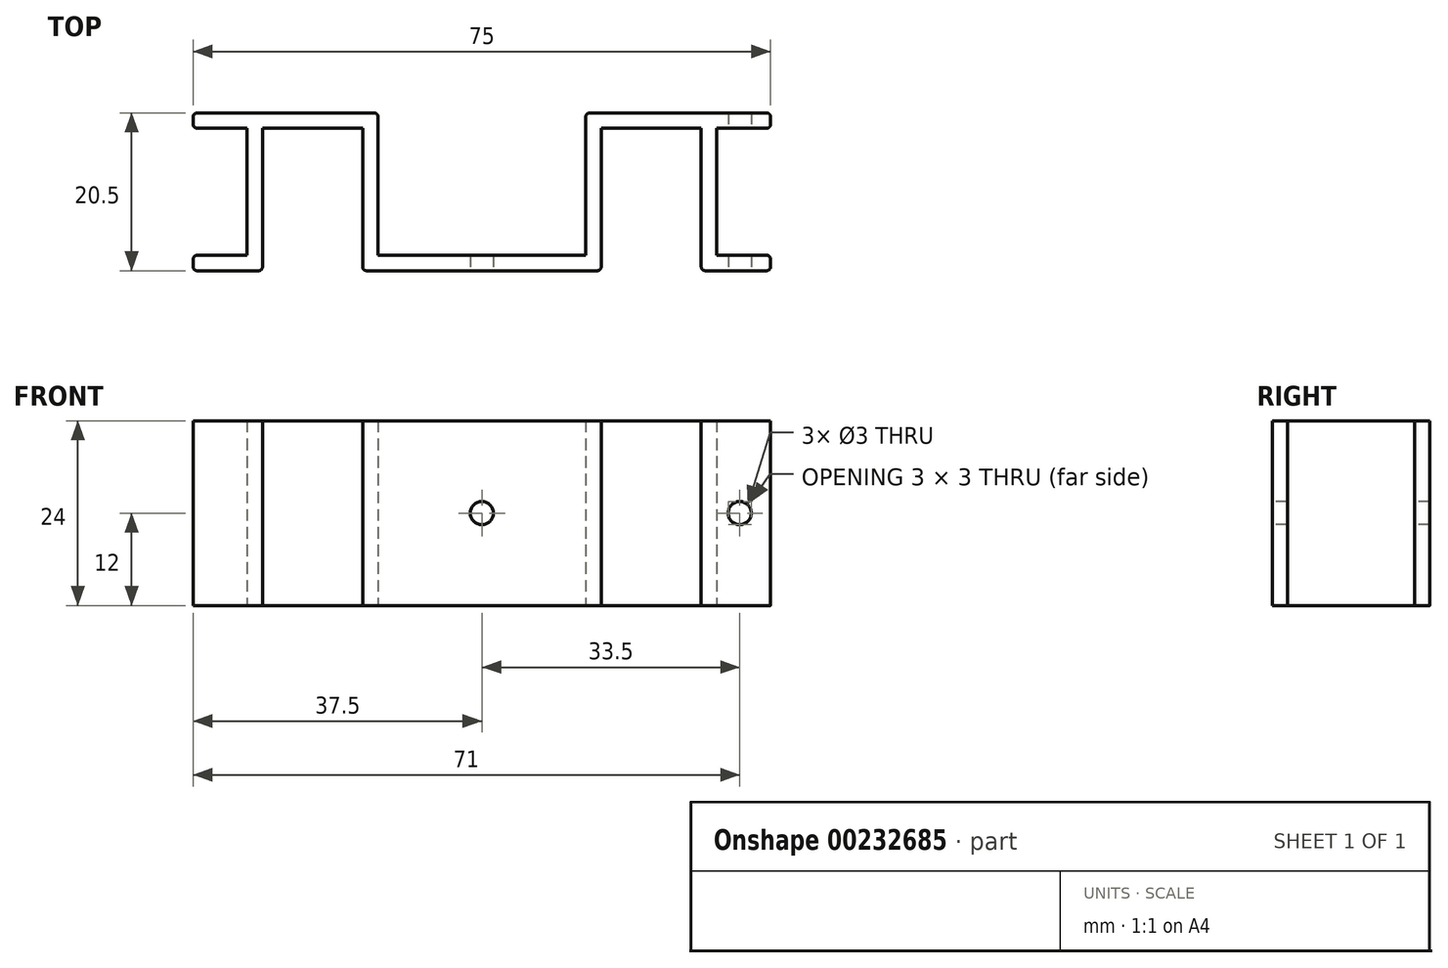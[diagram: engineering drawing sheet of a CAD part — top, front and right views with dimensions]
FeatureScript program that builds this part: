
annotation { "Feature Type Name" : "Feature", "Feature Type Description" : "" }
export const myFeature = defineFeature(function(context is Context, id is Id, definition is map)
    precondition{}
    {
        {
            var Q0;
            Q0=qCreatedBy(makeId("Top.planeOp"),FACE);
            var sketch = newSketch(context, id + "F0", { "sketchPlane" : qUnion([Q0])});
            skLineSegment(sketch, "E0", {"start": v(0, 0) * mm, "end": v(15.5, 0) * mm});
            skLineSegment(sketch, "E1", {"start": v(13.5, 20.5) * mm, "end": v(37.5, 20.5) * mm});
            skLineSegment(sketch, "E2", {"start": v(37.5, 20.5) * mm, "end": v(37.5, 18.5) * mm});
            skLineSegment(sketch, "E3", {"start": v(37.5, 18.5) * mm, "end": v(30.5, 18.5) * mm});
            skLineSegment(sketch, "E4", {"start": v(30.5, 18.5) * mm, "end": v(30.5, 2) * mm});
            skLineSegment(sketch, "E5", {"start": v(30.5, 2) * mm, "end": v(37.5, 2) * mm});
            skLineSegment(sketch, "E6", {"start": v(37.5, 2) * mm, "end": v(37.5, 0) * mm});
            skLineSegment(sketch, "E7", {"start": v(37.5, 0) * mm, "end": v(28.5, 0) * mm});
            skLineSegment(sketch, "E8", {"start": v(28.5, 0) * mm, "end": v(28.5, 18.5) * mm});
            skLineSegment(sketch, "E9", {"start": v(28.5, 18.5) * mm, "end": v(15.5, 18.5) * mm});
            skLineSegment(sketch, "E10", {"start": v(15.5, 18.5) * mm, "end": v(15.5, 0) * mm});
            skLineSegment(sketch, "E11", {"start": v(13.5, 2) * mm, "end": v(0, 2) * mm});
            skLineSegment(sketch, "E12", {"start": v(13.5, 2) * mm, "end": v(13.5, 20.5) * mm});
            skLineSegment(sketch, "E13.MirrorCS", {"start": v(0, 0) * mm, "end": v(-15.5, 0) * mm});
            skLineSegment(sketch, "E14.MirrorCS", {"start": v(-28.5, 18.5) * mm, "end": v(-15.5, 18.5) * mm});
            skLineSegment(sketch, "E15.MirrorCS", {"start": v(-37.5, 18.5) * mm, "end": v(-30.5, 18.5) * mm});
            skLineSegment(sketch, "E16.MirrorCS", {"start": v(-30.5, 2) * mm, "end": v(-37.5, 2) * mm});
            skLineSegment(sketch, "E17.MirrorCS", {"start": v(-15.5, 18.5) * mm, "end": v(-15.5, 0) * mm});
            skLineSegment(sketch, "E18.MirrorCS", {"start": v(-37.5, 2) * mm, "end": v(-37.5, 0) * mm});
            skLineSegment(sketch, "E19.MirrorCS", {"start": v(-37.5, 20.5) * mm, "end": v(-37.5, 18.5) * mm});
            skLineSegment(sketch, "E20.MirrorCS", {"start": v(-13.5, 2) * mm, "end": v(0, 2) * mm});
            skLineSegment(sketch, "E21.MirrorCS", {"start": v(-30.5, 18.5) * mm, "end": v(-30.5, 2) * mm});
            skLineSegment(sketch, "E22.MirrorCS", {"start": v(-28.5, 0) * mm, "end": v(-28.5, 18.5) * mm});
            skLineSegment(sketch, "E23.MirrorCS", {"start": v(-13.5, 2) * mm, "end": v(-13.5, 20.5) * mm});
            skLineSegment(sketch, "E24.MirrorCS", {"start": v(-13.5, 20.5) * mm, "end": v(-37.5, 20.5) * mm});
            skLineSegment(sketch, "E25.MirrorCS", {"start": v(-37.5, 0) * mm, "end": v(-28.5, 0) * mm});
            skPoint(sketch, "E26.orphan", {"position": v(0, 2) * mm});
            skSolve(sketch);
        }
        {
            var Q0;
            Q0=makeQuery(id+"F0.imprint","IMPRINT",FACE,{"disambiguationData":[TD([[makeQuery(id+"F0.imprint","IMPRINT",EDGE,{"derivedFrom":sQuery(id+"F0.wireOp",EDGE,"E0")}),1.0]])]});
            extrude(context, id + "F1", {"entities" : qUnion([Q0]), "depth" : 24 * mm});
        }
        {
            var Q0;
            Q0=makeQuery(id+"F1.opExtrude","SWEPT_FACE",FACE,{"disambiguationData":[OSD([sQuery(id+"F0.wireOp",EDGE,"E7")])]});
            var sketch = newSketch(context, id + "F2", { "sketchPlane" : qUnion([Q0])});
            skCircle(sketch, "E27", {"center": v(33.5, 12) * mm, "radius": 1.5 * mm});
            skCircle(sketch, "E28", {"center": v(0, 12) * mm, "radius": 1.5 * mm});
            skCircle(sketch, "E29.MirrorC", {"center": v(-33.5, 12) * mm, "radius": 1.5 * mm});
            skLineSegment(sketch, "E30", {"start": v(-41.57, 12) * mm, "end": v(-33.43, 12) * mm, "construction": true});
            skPoint(sketch, "E31", {"position": v(37.5, 12) * mm});
            skSolve(sketch);
        }
        {
            var Q0;
            Q0=makeQuery(id+"F2.imprint","IMPRINT",FACE,{"disambiguationData":[TD([[makeQuery(id+"F2.imprint","IMPRINT",EDGE,{"derivedFrom":sQuery(id+"F2.wireOp",EDGE,"E29.MirrorC")}),-1.0]])]});
            var Q1;
            Q1=makeQuery(id+"F2.imprint","IMPRINT",FACE,{"disambiguationData":[TD([[makeQuery(id+"F2.imprint","IMPRINT",EDGE,{"derivedFrom":sQuery(id+"F2.wireOp",EDGE,"E28")}),1.0]])]});
            var Q2;
            Q2=makeQuery(id+"F2.imprint","IMPRINT",FACE,{"disambiguationData":[TD([[makeQuery(id+"F2.imprint","IMPRINT",EDGE,{"derivedFrom":sQuery(id+"F2.wireOp",EDGE,"E27")}),1.0]])]});
            extrude(context, id + "F3", {"entities" : qUnion([Q0, Q1, Q2]), "operationType" : NewBodyOperationType.REMOVE, "oppositeDirection" : true, "depth" : 25 * mm});
        }
        {
            var Q0;
            Q0=makeQuery(id+"F1.opExtrude","SWEPT_EDGE",EDGE,{"disambiguationData":[OSD([sQuery(id+"F0.wireOp",EDGE,"E23.MirrorCS"),sQuery(id+"F0.wireOp",EDGE,"E24.MirrorCS")])]});
            var Q1;
            Q1=makeQuery(id+"F1.opExtrude","SWEPT_EDGE",EDGE,{"disambiguationData":[OSD([sQuery(id+"F0.wireOp",EDGE,"E1"),sQuery(id+"F0.wireOp",EDGE,"E12")])]});
            var Q2;
            Q2=makeQuery(id+"F1.opExtrude","SWEPT_EDGE",EDGE,{"disambiguationData":[OSD([sQuery(id+"F0.wireOp",EDGE,"E0"),sQuery(id+"F0.wireOp",EDGE,"E10")])]});
            var Q3;
            Q3=makeQuery(id+"F1.opExtrude","SWEPT_EDGE",EDGE,{"disambiguationData":[OSD([sQuery(id+"F0.wireOp",EDGE,"E22.MirrorCS"),sQuery(id+"F0.wireOp",EDGE,"E25.MirrorCS")])]});
            var Q4;
            Q4=makeQuery(id+"F1.opExtrude","SWEPT_EDGE",EDGE,{"disambiguationData":[OSD([sQuery(id+"F0.wireOp",EDGE,"E13.MirrorCS"),sQuery(id+"F0.wireOp",EDGE,"E17.MirrorCS")])]});
            var Q5;
            Q5=makeQuery(id+"F1.opExtrude","SWEPT_EDGE",EDGE,{"disambiguationData":[OSD([sQuery(id+"F0.wireOp",EDGE,"E7"),sQuery(id+"F0.wireOp",EDGE,"E8")])]});
            var Q6;
            Q6=makeQuery(id+"F1.opExtrude","SWEPT_EDGE",EDGE,{"disambiguationData":[OSD([sQuery(id+"F0.wireOp",EDGE,"E1"),sQuery(id+"F0.wireOp",EDGE,"E2")])]});
            var Q7;
            Q7=makeQuery(id+"F1.opExtrude","SWEPT_EDGE",EDGE,{"disambiguationData":[OSD([sQuery(id+"F0.wireOp",EDGE,"E2"),sQuery(id+"F0.wireOp",EDGE,"E3")])]});
            var Q8;
            Q8=makeQuery(id+"F1.opExtrude","SWEPT_EDGE",EDGE,{"disambiguationData":[OSD([sQuery(id+"F0.wireOp",EDGE,"E5"),sQuery(id+"F0.wireOp",EDGE,"E6")])]});
            var Q9;
            Q9=makeQuery(id+"F1.opExtrude","SWEPT_EDGE",EDGE,{"disambiguationData":[OSD([sQuery(id+"F0.wireOp",EDGE,"E6"),sQuery(id+"F0.wireOp",EDGE,"E7")])]});
            var Q10;
            Q10=makeQuery(id+"F1.opExtrude","SWEPT_EDGE",EDGE,{"disambiguationData":[OSD([sQuery(id+"F0.wireOp",EDGE,"E19.MirrorCS"),sQuery(id+"F0.wireOp",EDGE,"E24.MirrorCS")])]});
            var Q11;
            Q11=makeQuery(id+"F1.opExtrude","SWEPT_EDGE",EDGE,{"disambiguationData":[OSD([sQuery(id+"F0.wireOp",EDGE,"E15.MirrorCS"),sQuery(id+"F0.wireOp",EDGE,"E19.MirrorCS")])]});
            var Q12;
            Q12=makeQuery(id+"F1.opExtrude","SWEPT_EDGE",EDGE,{"disambiguationData":[OSD([sQuery(id+"F0.wireOp",EDGE,"E16.MirrorCS"),sQuery(id+"F0.wireOp",EDGE,"E18.MirrorCS")])]});
            var Q13;
            Q13=makeQuery(id+"F1.opExtrude","SWEPT_EDGE",EDGE,{"disambiguationData":[OSD([sQuery(id+"F0.wireOp",EDGE,"E18.MirrorCS"),sQuery(id+"F0.wireOp",EDGE,"E25.MirrorCS")])]});
            fillet(context, id + "F4", {"entities" : qUnion([Q0, Q1, Q2, Q3, Q4, Q5, Q6, Q7, Q8, Q9, Q10, Q11, Q12, Q13]), "radius" : .5 * mm, "tangentPropagation" : true, "allowEdgeOverflow" : false});
        }
    });
